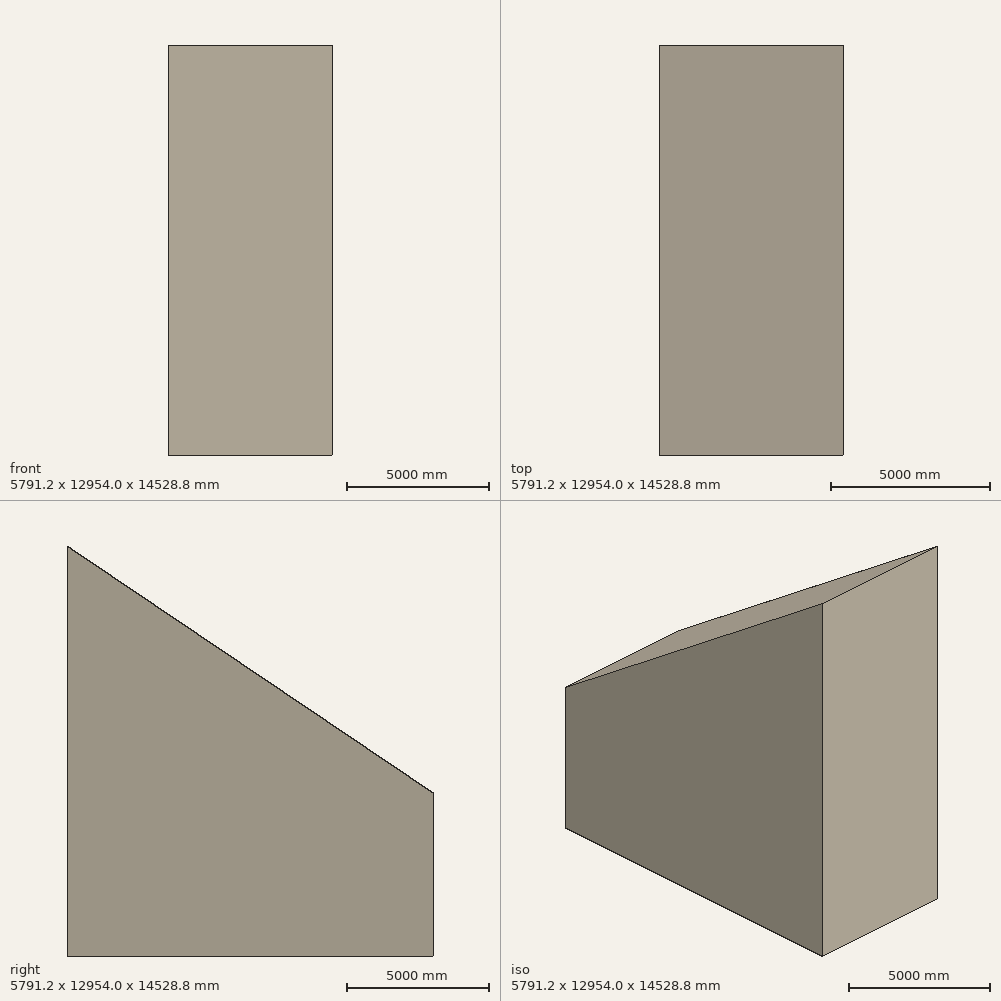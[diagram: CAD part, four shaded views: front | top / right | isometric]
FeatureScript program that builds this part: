
annotation { "Feature Type Name" : "Feature", "Feature Type Description" : "" }
export const myFeature = defineFeature(function(context is Context, id is Id, definition is map)
    precondition{}
    {
        {
            var Q0;
            Q0=qCreatedBy(makeId("Right.planeOp"),FACE);
            var sketch = newSketch(context, id + "F0", { "sketchPlane" : qUnion([Q0])});
            skLineSegment(sketch, "E0.bottom", {"start": v(6477, -2895.6) * mm, "end": v(-6477, -2895.6) * mm});
            skLineSegment(sketch, "E0.top", {"start": v(6477, 2895.6) * mm, "end": v(-6477, 2895.6) * mm});
            skLineSegment(sketch, "E0.left", {"start": v(6477, -2895.6) * mm, "end": v(6477, 2895.6) * mm});
            skLineSegment(sketch, "E0.right", {"start": v(-6477, -2895.6) * mm, "end": v(-6477, 2895.6) * mm});
            skPoint(sketch, "E0.middle", {"position": v(0, 0) * mm});
            skLineSegment(sketch, "E1", {"start": v(-6477, 2895.6) * mm, "end": v(-6477, 11633.18) * mm});
            skLineSegment(sketch, "E2", {"start": v(-6477, 11633.18) * mm, "end": v(6477, 2895.6) * mm});
            skSolve(sketch);
        }
        {
            var Q0;
            Q0=makeQuery(id+"F0.imprint","IMPRINT",FACE,{"disambiguationData":[TD([[makeQuery(id+"F0.imprint","IMPRINT",EDGE,{"derivedFrom":sQuery(id+"F0.wireOp",EDGE,"E0.bottom")}),-1.0]])]});
            var Q1;
            Q1=makeQuery(id+"F0.imprint","IMPRINT",FACE,{"disambiguationData":[TD([[makeQuery(id+"F0.imprint","IMPRINT",EDGE,{"derivedFrom":sQuery(id+"F0.wireOp",EDGE,"E0.top")}),-1.0]])]});
            extrude(context, id + "F1", {"entities" : qUnion([Q0, Q1]), "endBound" : BoundingType.SYMMETRIC, "depth" : 5791.2 * mm});
        }
    });
